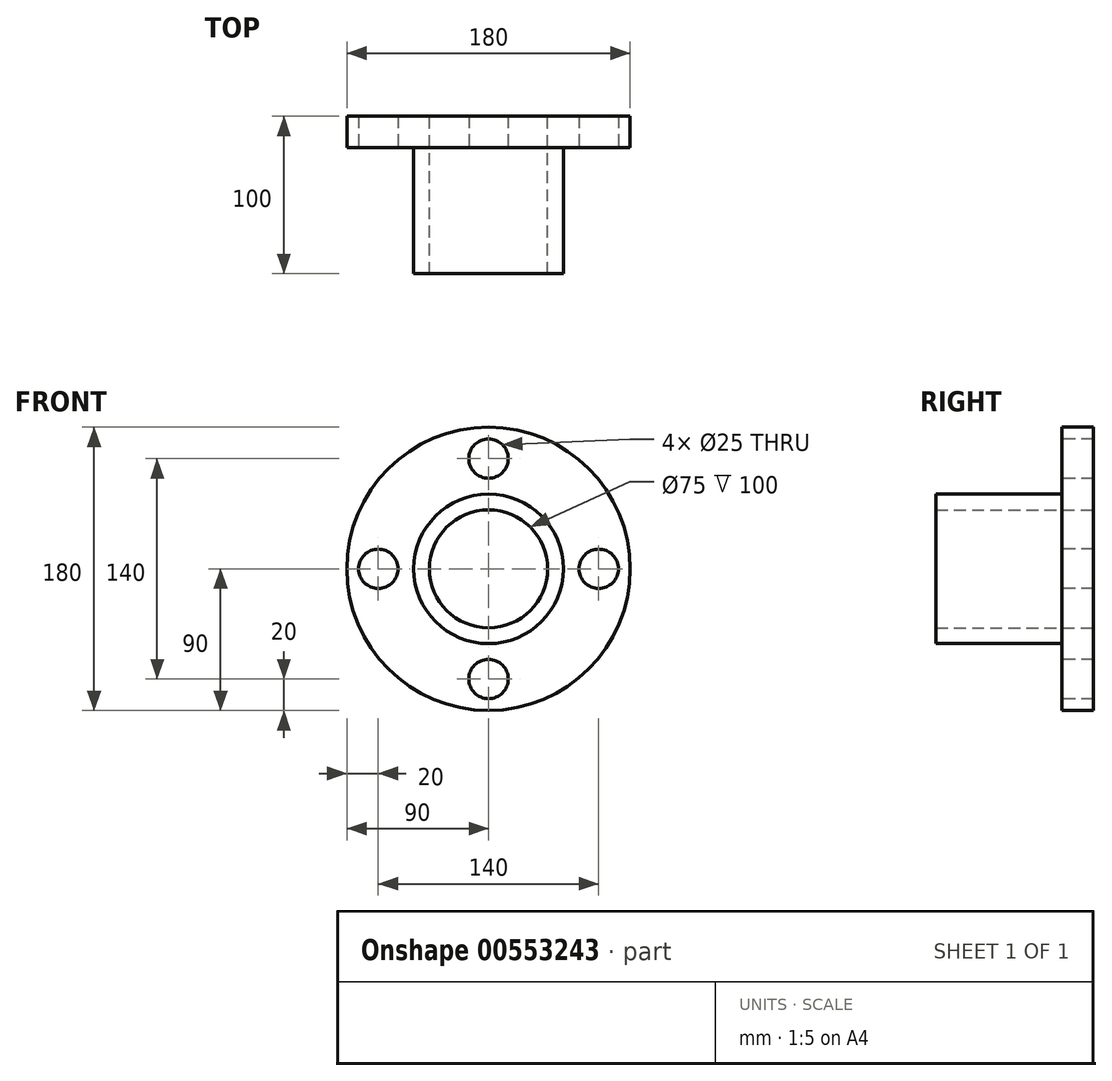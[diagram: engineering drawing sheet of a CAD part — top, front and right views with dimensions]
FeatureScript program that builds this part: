
annotation { "Feature Type Name" : "Feature", "Feature Type Description" : "" }
export const myFeature = defineFeature(function(context is Context, id is Id, definition is map)
    precondition{}
    {
        {
            var Q0;
            Q0=qCreatedBy(makeId("Right.planeOp"),FACE);
            var sketch = newSketch(context, id + "F0", { "sketchPlane" : qUnion([Q0])});
            skLineSegment(sketch, "E0", {"start": v(0, 0) * mm, "end": v(-106.62, 0) * mm, "construction": true});
            skLineSegment(sketch, "E1.bottom", {"start": v(0, 37.5) * mm, "end": v(-100, 37.5) * mm});
            skLineSegment(sketch, "E1.top", {"start": v(0, 90) * mm, "end": v(-20, 90) * mm});
            skLineSegment(sketch, "E1.left", {"start": v(0, 37.5) * mm, "end": v(0, 90) * mm});
            skLineSegment(sketch, "E1.right", {"start": v(-100, 37.5) * mm, "end": v(-100, 47.5) * mm});
            skLineSegment(sketch, "E2.top", {"start": v(-100, 47.5) * mm, "end": v(-20, 47.5) * mm});
            skLineSegment(sketch, "E2.right", {"start": v(-20, 90) * mm, "end": v(-20, 47.5) * mm});
            skSolve(sketch);
        }
        {
            var Q0;
            Q0=qSketchRegion(id+"F0",true);
            var Q1;
            Q1=sQuery(id+"F0.wireOp",EDGE,"E0");
            revolve(context, id + "F1", {"entities" : qUnion([Q0]), "axis" : qUnion([Q1]), "revolveType" : RevolveType.FULL});
        }
        {
            var Q0;
            Q0=makeQuery(id+"F1.opRevolve","SWEPT_FACE",FACE,{"disambiguationData":[OSD([sQuery(id+"F0.wireOp",EDGE,"E2.right")])]});
            var sketch = newSketch(context, id + "F2", { "sketchPlane" : qUnion([Q0])});
            skCircle(sketch, "E3", {"center": v(0, 70) * mm, "radius": 12.5 * mm});
            skSolve(sketch);
        }
        {
            var Q0;
            Q0=qSketchRegion(id+"F2",true);
            extrude(context, id + "F3", {"entities" : qUnion([Q0]), "operationType" : NewBodyOperationType.REMOVE, "endBound" : BoundingType.THROUGH_ALL, "oppositeDirection" : true, "depth" : 25 * mm});
        }
        {
            var Q0;
            Q0=makeQuery(id+"F3.boolean.opBoolean","COPY",FACE,{"derivedFrom":makeQuery(id+"F3.opExtrude","SWEPT_FACE",FACE,{"disambiguationData":[OSD([sQuery(id+"F2.wireOp",EDGE,"E3")])]})});
            var Q1;
            Q1=makeQuery(id+"F1.opRevolve","SWEPT_FACE",FACE,{"disambiguationData":[OSD([sQuery(id+"F0.wireOp",EDGE,"E1.bottom")])]});
            circularPattern(context, id + "F4", {"patternType" : PatternType.FACE, "faces" : qUnion([Q0]), "axis" : qUnion([Q1]), "angle" : 360 * degree, "instanceCount" : 4, "equalSpace" : true});
        }
    });
